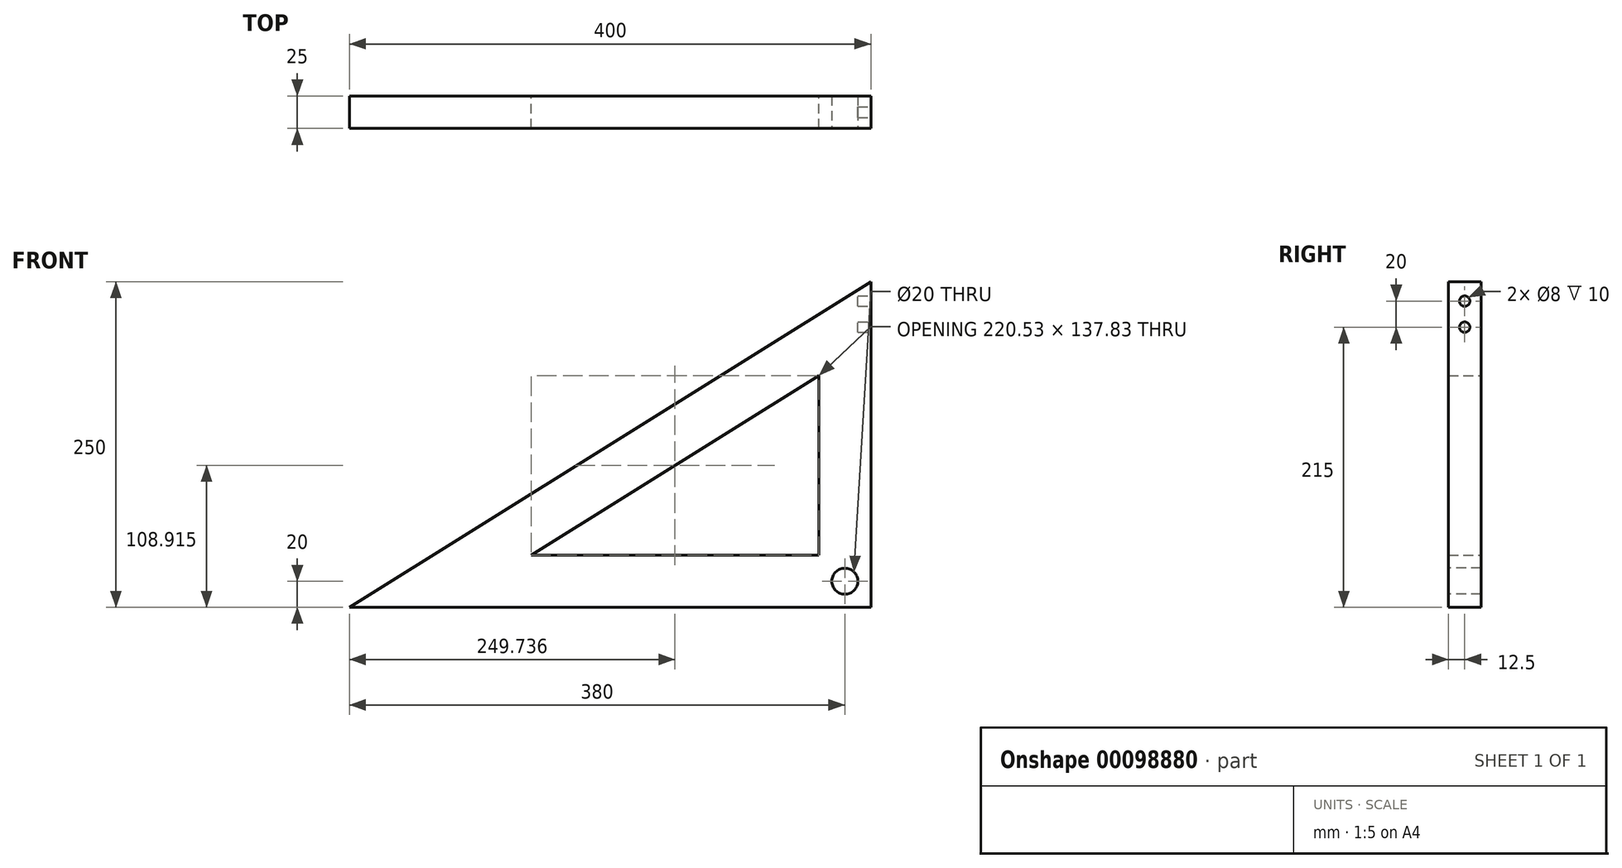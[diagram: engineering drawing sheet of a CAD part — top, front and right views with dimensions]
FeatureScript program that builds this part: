
annotation { "Feature Type Name" : "Feature", "Feature Type Description" : "" }
export const myFeature = defineFeature(function(context is Context, id is Id, definition is map)
    precondition{}
    {
        {
            var Q0;
            Q0=qCreatedBy(makeId("Front.planeOp"),FACE);
            var sketch = newSketch(context, id + "F0", { "sketchPlane" : qUnion([Q0])});
            skLineSegment(sketch, "E0", {"start": v(0, 0) * mm, "end": v(-400, 0) * mm});
            skLineSegment(sketch, "E1", {"start": v(0, 0) * mm, "end": v(0, 250) * mm});
            skLineSegment(sketch, "E2", {"start": v(0, 250) * mm, "end": v(-400, 0) * mm});
            skLineSegment(sketch, "E3.0", {"start": v(-40, 177.83) * mm, "end": v(-260.53, 40) * mm});
            skLineSegment(sketch, "E4.0", {"start": v(-40, 40) * mm, "end": v(-40, 177.83) * mm});
            skLineSegment(sketch, "E5.0", {"start": v(-40, 40) * mm, "end": v(-260.53, 40) * mm});
            skSolve(sketch);
        }
        {
            var Q0;
            Q0=makeQuery(id+"F0.imprint","IMPRINT",FACE,{"disambiguationData":[TD([[makeQuery(id+"F0.imprint","IMPRINT",EDGE,{"derivedFrom":sQuery(id+"F0.wireOp",EDGE,"E0")}),-1.0]])]});
            extrude(context, id + "F1", {"entities" : qUnion([Q0]), "depth" : 25 * mm});
        }
        {
            var Q0;
            Q0=qCreatedBy(makeId("Right.planeOp"),FACE);
            var sketch = newSketch(context, id + "F2", { "sketchPlane" : qUnion([Q0])});
            skLineSegment(sketch, "E6", {"start": v(0, 0) * mm, "end": v(-12.5, 0) * mm});
            skCircle(sketch, "E7", {"center": v(-12.5, 235) * mm, "radius": 4 * mm});
            skCircle(sketch, "E8", {"center": v(-12.5, 215) * mm, "radius": 4 * mm});
            skSolve(sketch);
        }
        {
            var Q0;
            Q0=makeQuery(id+"F2.imprint","IMPRINT",FACE,{"disambiguationData":[TD([[makeQuery(id+"F2.imprint","IMPRINT",EDGE,{"derivedFrom":sQuery(id+"F2.wireOp",EDGE,"E7")}),1.0]])]});
            var Q1;
            Q1=makeQuery(id+"F2.imprint","IMPRINT",FACE,{"disambiguationData":[TD([[makeQuery(id+"F2.imprint","IMPRINT",EDGE,{"derivedFrom":sQuery(id+"F2.wireOp",EDGE,"E8")}),1.0]])]});
            extrude(context, id + "F3", {"entities" : qUnion([Q0, Q1]), "operationType" : NewBodyOperationType.REMOVE, "oppositeDirection" : true, "depth" : 10 * mm});
        }
        {
            var Q0;
            Q0=makeQuery(id+"F1.opExtrude","CAP_FACE",FACE,{"disambiguationData":[OSD([sQuery(id+"F0.wireOp",EDGE,"E0"),sQuery(id+"F0.wireOp",EDGE,"E1"),sQuery(id+"F0.wireOp",EDGE,"E2"),sQuery(id+"F0.wireOp",EDGE,"E3.0"),sQuery(id+"F0.wireOp",EDGE,"E4.0"),sQuery(id+"F0.wireOp",EDGE,"E5.0")])],"isStart":false});
            var sketch = newSketch(context, id + "F4", { "sketchPlane" : qUnion([Q0])});
            skCircle(sketch, "E9", {"center": v(-20, 20) * mm, "radius": 10 * mm});
            skSolve(sketch);
        }
        {
            var Q0;
            Q0=makeQuery(id+"F4.imprint","IMPRINT",FACE,{"disambiguationData":[TD([[makeQuery(id+"F4.imprint","IMPRINT",EDGE,{"derivedFrom":sQuery(id+"F4.wireOp",EDGE,"E9")}),1.0]])]});
            extrude(context, id + "F5", {"entities" : qUnion([Q0]), "operationType" : NewBodyOperationType.REMOVE, "endBound" : BoundingType.UP_TO_NEXT, "oppositeDirection" : true, "depth" : 25 * mm});
        }
    });
